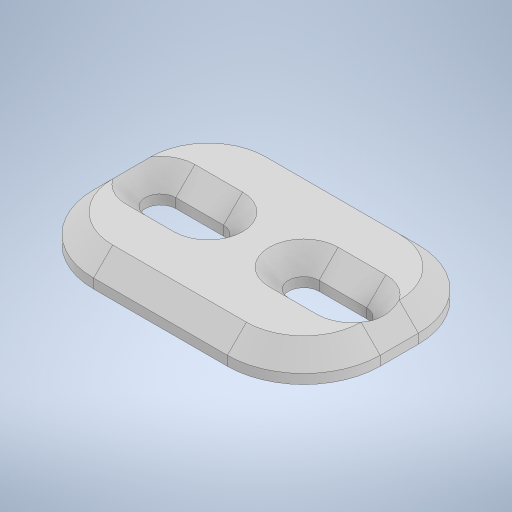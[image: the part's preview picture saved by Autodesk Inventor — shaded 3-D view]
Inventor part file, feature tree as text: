
AUTODESK INVENTOR PART (.ipt)
format: ipt  version: 2024.1 (Build 281209000, 209)  size: 309,760 bytes
history: native  units: in
note: dims shown in document units (in); Inventor stores cm internally (conversion verified against a paired STEP export)
features: extrude x2, chamfer x2, sketch x2, other x1, fillet x1
ambient origin geometry x8: Origin, YZ Plane, XZ Plane, XY Plane, X Axis, Y Axis, Z Axis, Center Point
bodies: Body1 (feature_tree)
feature tree (8):
  other  "bracket"
  extrude  "Extrusion1"  Depth=1.1811in
  extrude  "Extrusion6"  Depth=0.3937in
  fillet  "Fillet5"  Radius=0.3937in
  chamfer  "Chamfer5"  Distance=0.126in
  chamfer  "Chamfer6"  Distance=0.1969in
  sketch  "Sketch1"  dims[d0=0.7874in d1=1.1811in]
  sketch  "Sketch10"  dims[d2=0.1181in d3=0.0in d64=0.7874in d65=0.3937in d66=0.126in d67=0.1969in d68=0.7874in d69=0.1969in d70=0.0in d71=0.0in d72=0.315in d73=0.0787in d74=0.0787in d75=45.0deg d76=0.0787in d77=0.0787in d78=45.0deg d79=0.1969in d80=0.1969in]
